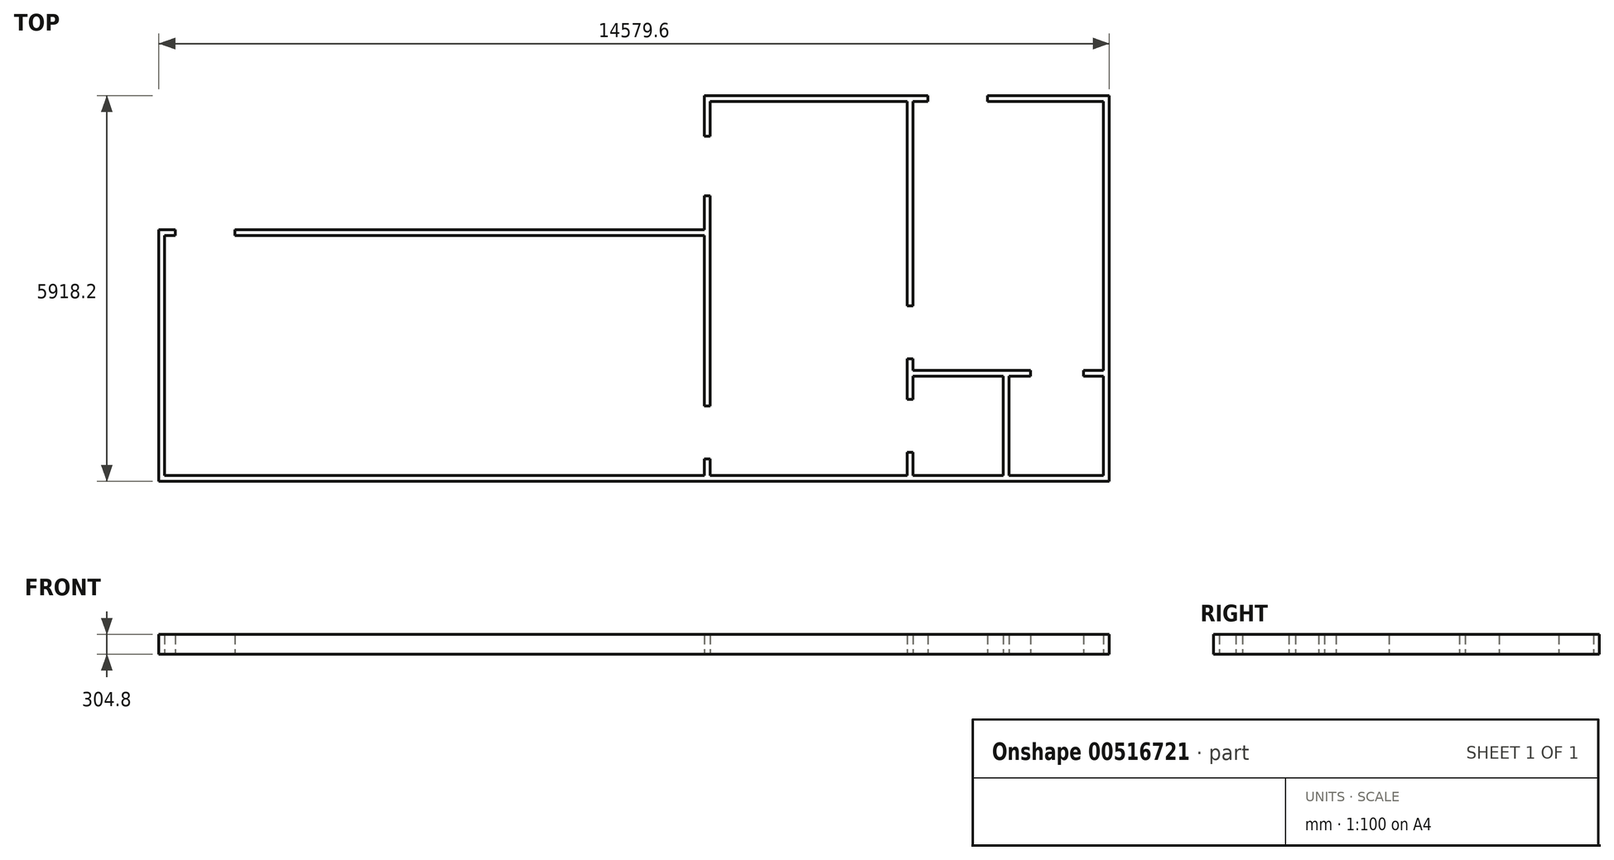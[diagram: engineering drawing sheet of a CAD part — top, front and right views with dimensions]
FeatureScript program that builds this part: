
annotation { "Feature Type Name" : "Feature", "Feature Type Description" : "" }
export const myFeature = defineFeature(function(context is Context, id is Id, definition is map)
    precondition{}
    {
        {
            var Q0;
            Q0=qCreatedBy(makeId("Top.planeOp"),FACE);
            var sketch = newSketch(context, id + "F0", { "sketchPlane" : qUnion([Q0])});
            skLineSegment(sketch, "E0", {"start": v(0, 0) * mm, "end": v(14579.6, 0) * mm});
            skLineSegment(sketch, "E1", {"start": v(14579.6, 0) * mm, "end": v(14579.6, 5918.2) * mm});
            skLineSegment(sketch, "E2", {"start": v(14579.6, 5918.2) * mm, "end": v(8369.3, 5918.2) * mm});
            skLineSegment(sketch, "E3", {"start": v(8369.3, 5918.2) * mm, "end": v(8369.3, 3860.8) * mm});
            skLineSegment(sketch, "E4", {"start": v(8369.3, 3860.8) * mm, "end": v(0, 3860.8) * mm});
            skLineSegment(sketch, "E5", {"start": v(0, 3860.8) * mm, "end": v(0, 0) * mm});
            skLineSegment(sketch, "E6", {"start": v(88.9, 88.9) * mm, "end": v(88.9, 3771.9) * mm});
            skLineSegment(sketch, "E7", {"start": v(88.9, 3771.9) * mm, "end": v(8369.3, 3771.9) * mm});
            skLineSegment(sketch, "E8", {"start": v(8369.3, 3771.9) * mm, "end": v(8369.3, 88.9) * mm});
            skLineSegment(sketch, "E9", {"start": v(8369.3, 88.9) * mm, "end": v(88.9, 88.9) * mm});
            skLineSegment(sketch, "E10", {"start": v(8458.2, 88.9) * mm, "end": v(8458.2, 5829.3) * mm});
            skLineSegment(sketch, "E11", {"start": v(8458.2, 5829.3) * mm, "end": v(11480.8, 5829.3) * mm});
            skLineSegment(sketch, "E12", {"start": v(8458.2, 88.9) * mm, "end": v(11480.8, 88.9) * mm});
            skLineSegment(sketch, "E13", {"start": v(11480.8, 88.9) * mm, "end": v(11480.8, 5829.3) * mm});
            skLineSegment(sketch, "E14", {"start": v(11569.7, 5829.3) * mm, "end": v(11569.7, 1701.8) * mm});
            skLineSegment(sketch, "E15", {"start": v(11569.7, 88.9) * mm, "end": v(12954, 88.9) * mm});
            skLineSegment(sketch, "E16", {"start": v(14490.7, 88.9) * mm, "end": v(14490.7, 1612.9) * mm});
            skLineSegment(sketch, "E17", {"start": v(14490.7, 5829.3) * mm, "end": v(11569.7, 5829.3) * mm});
            skLineSegment(sketch, "E18", {"start": v(11569.7, 1701.8) * mm, "end": v(14490.7, 1701.8) * mm});
            skLineSegment(sketch, "E19", {"start": v(11569.7, 1612.9) * mm, "end": v(12954, 1612.9) * mm});
            skLineSegment(sketch, "E20.trimOffspring", {"start": v(11569.7, 1612.9) * mm, "end": v(11569.7, 88.9) * mm});
            skLineSegment(sketch, "E21.trimOffspring", {"start": v(14490.7, 1701.8) * mm, "end": v(14490.7, 5829.3) * mm});
            skLineSegment(sketch, "E22", {"start": v(12954, 1612.9) * mm, "end": v(12954, 88.9) * mm});
            skLineSegment(sketch, "E23", {"start": v(13042.9, 1612.9) * mm, "end": v(13042.9, 88.9) * mm});
            skLineSegment(sketch, "E24.trimOffspring", {"start": v(13042.9, 1612.9) * mm, "end": v(14490.7, 1612.9) * mm});
            skLineSegment(sketch, "E25.trimOffspring", {"start": v(13042.9, 88.9) * mm, "end": v(14490.7, 88.9) * mm});
            skSolve(sketch);
        }
        {
            var Q0;
            Q0 = qSketchRegion(id + "F0", true);
            extrude(context, id + "F1", {"entities" : qUnion([Q0]), "depth" : 2387.6 * mm, "offsetDistance" : 25.4 * mm});
        }
        {
            var Q0;
            Q0=qCreatedBy(makeId("Top.planeOp"),FACE);
            var sketch = newSketch(context, id + "F2", { "sketchPlane" : qUnion([Q0])});
            skLineSegment(sketch, "E26.bottom", {"start": v(254, 3860.8) * mm, "end": v(1168.4, 3860.8) * mm});
            skLineSegment(sketch, "E26.top", {"start": v(254, 3771.9) * mm, "end": v(1168.4, 3771.9) * mm});
            skLineSegment(sketch, "E26.left", {"start": v(254, 3860.8) * mm, "end": v(254, 3771.9) * mm});
            skLineSegment(sketch, "E26.right", {"start": v(1168.4, 3860.8) * mm, "end": v(1168.4, 3771.9) * mm});
            skLineSegment(sketch, "E27.bottom", {"start": v(2197.1, 3860.8) * mm, "end": v(3416.3, 3860.8) * mm});
            skLineSegment(sketch, "E27.top", {"start": v(2197.1, 3771.9) * mm, "end": v(3416.3, 3771.9) * mm});
            skLineSegment(sketch, "E27.left", {"start": v(2197.1, 3860.8) * mm, "end": v(2197.1, 3771.9) * mm});
            skLineSegment(sketch, "E27.right", {"start": v(3416.3, 3860.8) * mm, "end": v(3416.3, 3771.9) * mm});
            skLineSegment(sketch, "E28.bottom", {"start": v(5702.3, 3860.8) * mm, "end": v(6921.5, 3860.8) * mm});
            skLineSegment(sketch, "E28.top", {"start": v(5702.3, 3771.9) * mm, "end": v(6921.5, 3771.9) * mm});
            skLineSegment(sketch, "E28.left", {"start": v(5702.3, 3860.8) * mm, "end": v(5702.3, 3771.9) * mm});
            skLineSegment(sketch, "E28.right", {"start": v(6921.5, 3860.8) * mm, "end": v(6921.5, 3771.9) * mm});
            skLineSegment(sketch, "E29.bottom", {"start": v(8369.3, 1155.7) * mm, "end": v(8458.2, 1155.7) * mm});
            skLineSegment(sketch, "E29.top", {"start": v(8369.3, 342.9) * mm, "end": v(8458.2, 342.9) * mm});
            skLineSegment(sketch, "E29.left", {"start": v(8369.3, 1155.7) * mm, "end": v(8369.3, 342.9) * mm});
            skLineSegment(sketch, "E29.right", {"start": v(8458.2, 1155.7) * mm, "end": v(8458.2, 342.9) * mm});
            skLineSegment(sketch, "E30.bottom", {"start": v(9372.6, 5918.2) * mm, "end": v(10591.8, 5918.2) * mm});
            skLineSegment(sketch, "E30.top", {"start": v(9372.6, 5829.3) * mm, "end": v(10591.8, 5829.3) * mm});
            skLineSegment(sketch, "E30.left", {"start": v(9372.6, 5918.2) * mm, "end": v(9372.6, 5829.3) * mm});
            skLineSegment(sketch, "E30.right", {"start": v(10591.8, 5918.2) * mm, "end": v(10591.8, 5829.3) * mm});
            skLineSegment(sketch, "E31.bottom", {"start": v(11798.3, 5918.2) * mm, "end": v(12712.7, 5918.2) * mm});
            skLineSegment(sketch, "E31.top", {"start": v(11798.3, 5829.3) * mm, "end": v(12712.7, 5829.3) * mm});
            skLineSegment(sketch, "E31.left", {"start": v(11798.3, 5918.2) * mm, "end": v(11798.3, 5829.3) * mm});
            skLineSegment(sketch, "E31.right", {"start": v(12712.7, 5918.2) * mm, "end": v(12712.7, 5829.3) * mm});
            skLineSegment(sketch, "E32.bottom", {"start": v(13042.9, 5918.2) * mm, "end": v(14262.1, 5918.2) * mm});
            skLineSegment(sketch, "E32.top", {"start": v(13042.9, 5829.3) * mm, "end": v(14262.1, 5829.3) * mm});
            skLineSegment(sketch, "E32.left", {"start": v(13042.9, 5918.2) * mm, "end": v(13042.9, 5829.3) * mm});
            skLineSegment(sketch, "E32.right", {"start": v(14262.1, 5918.2) * mm, "end": v(14262.1, 5829.3) * mm});
            skLineSegment(sketch, "E33.bottom", {"start": v(8369.3, 5295.9) * mm, "end": v(8458.2, 5295.9) * mm});
            skLineSegment(sketch, "E33.top", {"start": v(8369.3, 4381.5) * mm, "end": v(8458.2, 4381.5) * mm});
            skLineSegment(sketch, "E33.left", {"start": v(8369.3, 5295.9) * mm, "end": v(8369.3, 4381.5) * mm});
            skLineSegment(sketch, "E33.right", {"start": v(8458.2, 5295.9) * mm, "end": v(8458.2, 4381.5) * mm});
            skLineSegment(sketch, "E34.bottom", {"start": v(11480.8, 1257.3) * mm, "end": v(11569.7, 1257.3) * mm});
            skLineSegment(sketch, "E34.top", {"start": v(11480.8, 444.5) * mm, "end": v(11569.7, 444.5) * mm});
            skLineSegment(sketch, "E34.left", {"start": v(11480.8, 1257.3) * mm, "end": v(11480.8, 444.5) * mm});
            skLineSegment(sketch, "E34.right", {"start": v(11569.7, 1257.3) * mm, "end": v(11569.7, 444.5) * mm});
            skLineSegment(sketch, "E35.bottom", {"start": v(13373.1, 1701.8) * mm, "end": v(14185.9, 1701.8) * mm});
            skLineSegment(sketch, "E35.top", {"start": v(13373.1, 1612.9) * mm, "end": v(14185.9, 1612.9) * mm});
            skLineSegment(sketch, "E35.left", {"start": v(13373.1, 1701.8) * mm, "end": v(13373.1, 1612.9) * mm});
            skLineSegment(sketch, "E35.right", {"start": v(14185.9, 1701.8) * mm, "end": v(14185.9, 1612.9) * mm});
            skLineSegment(sketch, "E36.bottom", {"start": v(14490.7, 5575.3) * mm, "end": v(14579.6, 5575.3) * mm});
            skLineSegment(sketch, "E36.top", {"start": v(14490.7, 4356.1) * mm, "end": v(14579.6, 4356.1) * mm});
            skLineSegment(sketch, "E36.left", {"start": v(14490.7, 5575.3) * mm, "end": v(14490.7, 4356.1) * mm});
            skLineSegment(sketch, "E36.right", {"start": v(14579.6, 5575.3) * mm, "end": v(14579.6, 4356.1) * mm});
            skLineSegment(sketch, "E37.bottom", {"start": v(9042.4, 88.9) * mm, "end": v(10744.2, 88.9) * mm});
            skLineSegment(sketch, "E37.top", {"start": v(9042.4, 0) * mm, "end": v(10744.2, 0) * mm});
            skLineSegment(sketch, "E37.left", {"start": v(9042.4, 88.9) * mm, "end": v(9042.4, 0) * mm});
            skLineSegment(sketch, "E37.right", {"start": v(10744.2, 88.9) * mm, "end": v(10744.2, 0) * mm});
            skLineSegment(sketch, "E38.bottom", {"start": v(11480.8, 2692.4) * mm, "end": v(11569.7, 2692.4) * mm});
            skLineSegment(sketch, "E38.top", {"start": v(11480.8, 1879.6) * mm, "end": v(11569.7, 1879.6) * mm});
            skLineSegment(sketch, "E38.left", {"start": v(11480.8, 2692.4) * mm, "end": v(11480.8, 1879.6) * mm});
            skLineSegment(sketch, "E38.right", {"start": v(11569.7, 2692.4) * mm, "end": v(11569.7, 1879.6) * mm});
            skSolve(sketch);
        }
        {
            var Q0;
            Q0=makeQuery(id+"F2.imprint","IMPRINT",FACE,{"disambiguationData":[TD([[makeQuery(id+"F2.imprint","IMPRINT",EDGE,{"derivedFrom":sQuery(id+"F2.wireOp",EDGE,"E26.bottom")}),-1.0]])]});
            var Q1;
            Q1=makeQuery(id+"F2.imprint","IMPRINT",FACE,{"disambiguationData":[TD([[makeQuery(id+"F2.imprint","IMPRINT",EDGE,{"derivedFrom":sQuery(id+"F2.wireOp",EDGE,"E29.bottom")}),-1.0]])]});
            var Q2;
            Q2=makeQuery(id+"F2.imprint","IMPRINT",FACE,{"disambiguationData":[TD([[makeQuery(id+"F2.imprint","IMPRINT",EDGE,{"derivedFrom":sQuery(id+"F2.wireOp",EDGE,"E33.bottom")}),-1.0]])]});
            var Q3;
            Q3=makeQuery(id+"F2.imprint","IMPRINT",FACE,{"disambiguationData":[TD([[makeQuery(id+"F2.imprint","IMPRINT",EDGE,{"derivedFrom":sQuery(id+"F2.wireOp",EDGE,"E31.bottom")}),-1.0]])]});
            var Q4;
            Q4=makeQuery(id+"F2.imprint","IMPRINT",FACE,{"disambiguationData":[TD([[makeQuery(id+"F2.imprint","IMPRINT",EDGE,{"derivedFrom":sQuery(id+"F2.wireOp",EDGE,"E34.bottom")}),-1.0]])]});
            var Q5;
            Q5=makeQuery(id+"F2.imprint","IMPRINT",FACE,{"disambiguationData":[TD([[makeQuery(id+"F2.imprint","IMPRINT",EDGE,{"derivedFrom":sQuery(id+"F2.wireOp",EDGE,"E35.bottom")}),-1.0]])]});
            var Q6;
            Q6=makeQuery(id+"F2.imprint","IMPRINT",FACE,{"disambiguationData":[TD([[makeQuery(id+"F2.imprint","IMPRINT",EDGE,{"derivedFrom":sQuery(id+"F2.wireOp",EDGE,"E38.bottom")}),-1.0]])]});
            extrude(context, id + "F3", {"entities" : qUnion([Q0, Q1, Q2, Q3, Q4, Q5, Q6]), "operationType" : NewBodyOperationType.REMOVE, "depth" : 2032 * mm, "offsetDistance" : 25.4 * mm});
        }
        {
            var Q0;
            Q0=qCreatedBy(makeId("Top.planeOp"),FACE);
            cPlane(context, id + "F4", {"entities" : qUnion([Q0]), "cplaneType" : CPlaneType.OFFSET, "offset" : 965.2 * mm, "width" : 152.4 * mm, "height" : 152.4 * mm});
        }
        {
            var Q0;
            Q0=qCreatedBy(id+"F4.planeOp",FACE);
            var sketch = newSketch(context, id + "F5", { "sketchPlane" : qUnion([Q0])});
            skLineSegment(sketch, "E39.4", {"start": v(2197.1, 3860.8) * mm, "end": v(3416.3, 3860.8) * mm});
            skLineSegment(sketch, "E39.5", {"start": v(2197.1, 3771.9) * mm, "end": v(3416.3, 3771.9) * mm});
            skLineSegment(sketch, "E39.6", {"start": v(2197.1, 3860.8) * mm, "end": v(2197.1, 3771.9) * mm});
            skLineSegment(sketch, "E39.7", {"start": v(3416.3, 3860.8) * mm, "end": v(3416.3, 3771.9) * mm});
            skLineSegment(sketch, "E39.8", {"start": v(5702.3, 3860.8) * mm, "end": v(6921.5, 3860.8) * mm});
            skLineSegment(sketch, "E39.9", {"start": v(5702.3, 3771.9) * mm, "end": v(6921.5, 3771.9) * mm});
            skLineSegment(sketch, "E39.10", {"start": v(5702.3, 3860.8) * mm, "end": v(5702.3, 3771.9) * mm});
            skLineSegment(sketch, "E39.11", {"start": v(6921.5, 3860.8) * mm, "end": v(6921.5, 3771.9) * mm});
            skLineSegment(sketch, "E39.16", {"start": v(9372.6, 5918.2) * mm, "end": v(10591.8, 5918.2) * mm});
            skLineSegment(sketch, "E39.17", {"start": v(9372.6, 5829.3) * mm, "end": v(10591.8, 5829.3) * mm});
            skLineSegment(sketch, "E39.18", {"start": v(9372.6, 5918.2) * mm, "end": v(9372.6, 5829.3) * mm});
            skLineSegment(sketch, "E39.19", {"start": v(10591.8, 5918.2) * mm, "end": v(10591.8, 5829.3) * mm});
            skLineSegment(sketch, "E39.24", {"start": v(13042.9, 5918.2) * mm, "end": v(14262.1, 5918.2) * mm});
            skLineSegment(sketch, "E39.25", {"start": v(13042.9, 5829.3) * mm, "end": v(14262.1, 5829.3) * mm});
            skLineSegment(sketch, "E39.26", {"start": v(13042.9, 5918.2) * mm, "end": v(13042.9, 5829.3) * mm});
            skLineSegment(sketch, "E39.27", {"start": v(14262.1, 5918.2) * mm, "end": v(14262.1, 5829.3) * mm});
            skLineSegment(sketch, "E39.40", {"start": v(14490.7, 5575.3) * mm, "end": v(14579.6, 5575.3) * mm});
            skLineSegment(sketch, "E39.41", {"start": v(14490.7, 4356.1) * mm, "end": v(14579.6, 4356.1) * mm});
            skLineSegment(sketch, "E39.42", {"start": v(14490.7, 5575.3) * mm, "end": v(14490.7, 4356.1) * mm});
            skLineSegment(sketch, "E39.43", {"start": v(14579.6, 5575.3) * mm, "end": v(14579.6, 4356.1) * mm});
            skLineSegment(sketch, "E40.0", {"start": v(9042.4, 88.9) * mm, "end": v(10744.2, 88.9) * mm});
            skLineSegment(sketch, "E40.1", {"start": v(10744.2, 88.9) * mm, "end": v(10744.2, 0) * mm});
            skLineSegment(sketch, "E40.2", {"start": v(9042.4, 0) * mm, "end": v(10744.2, 0) * mm});
            skLineSegment(sketch, "E40.3", {"start": v(9042.4, 88.9) * mm, "end": v(9042.4, 0) * mm});
            skSolve(sketch);
        }
        {
            var Q0;
            Q0=qCreatedBy(makeId("Top.planeOp"),FACE);
            cPlane(context, id + "F6", {"entities" : qUnion([Q0]), "cplaneType" : CPlaneType.OFFSET, "offset" : 1879.6 * mm, "width" : 152.4 * mm, "height" : 152.4 * mm});
        }
        {
            var Q0;
            Q0 = qSketchRegion(id + "F5", true);
            var Q1;
            Q1=qCreatedBy(id+"F6.planeOp",FACE);
            extrude(context, id + "F7", {"entities" : qUnion([Q0]), "operationType" : NewBodyOperationType.REMOVE, "endBound" : BoundingType.UP_TO_SURFACE, "depth" : 25.4 * mm, "endBoundEntityFace" : qUnion([Q1]), "offsetDistance" : 25.4 * mm});
        }
        {
            var Q0;
            Q0=qCreatedBy(makeId("Top.planeOp"),FACE);
            cPlane(context, id + "F8", {"entities" : qUnion([Q0]), "cplaneType" : CPlaneType.OFFSET, "offset" : 304.8 * mm, "width" : 152.4 * mm, "height" : 152.4 * mm});
        }
        {
            var Q0;
            Q0=qCreatedBy(id+"F8.planeOp",FACE);
            var sketch = newSketch(context, id + "F9", { "sketchPlane" : qUnion([Q0])});
            skLineSegment(sketch, "E41.bottom", {"start": v(0, 0) * mm, "end": v(14579.6, 0) * mm});
            skLineSegment(sketch, "E41.top", {"start": v(0, 5918.2) * mm, "end": v(14579.6, 5918.2) * mm});
            skLineSegment(sketch, "E41.left", {"start": v(0, 0) * mm, "end": v(0, 5918.2) * mm});
            skLineSegment(sketch, "E41.right", {"start": v(14579.6, 0) * mm, "end": v(14579.6, 5918.2) * mm});
            skSolve(sketch);
        }
        {
            var Q0;
            Q0 = qSketchRegion(id + "F9", true);
            extrude(context, id + "F10", {"entities" : qUnion([Q0]), "operationType" : NewBodyOperationType.REMOVE, "endBound" : BoundingType.THROUGH_ALL, "depth" : 25.4 * mm, "offsetDistance" : 25.4 * mm});
        }
    });
